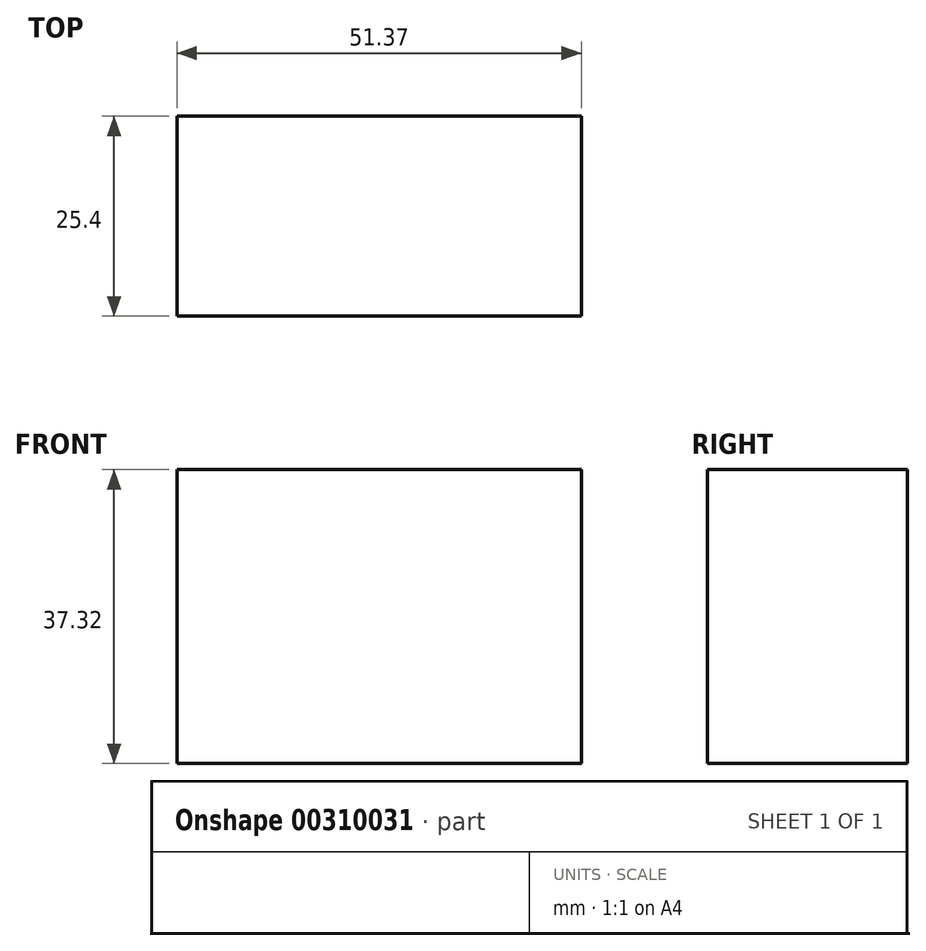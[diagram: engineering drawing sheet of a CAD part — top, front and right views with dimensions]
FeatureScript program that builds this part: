
annotation { "Feature Type Name" : "Feature", "Feature Type Description" : "" }
export const myFeature = defineFeature(function(context is Context, id is Id, definition is map)
    precondition{}
    {
        {
            var Q0;
            Q0=qCreatedBy(makeId("Front.planeOp"),FACE);
            var sketch = newSketch(context, id + "F0", { "sketchPlane" : qUnion([Q0])});
            skLineSegment(sketch, "E0", {"start": v(0, 0) * mm, "end": v(0, 37.32) * mm});
            skLineSegment(sketch, "E1", {"start": v(0, 37.32) * mm, "end": v(51.37, 37.32) * mm});
            skLineSegment(sketch, "E2", {"start": v(51.37, 37.32) * mm, "end": v(51.37, 0) * mm});
            skLineSegment(sketch, "E3", {"start": v(51.37, 0) * mm, "end": v(0, 0) * mm});
            skSolve(sketch);
        }
        {
            var Q0;
            Q0 = qSketchRegion(id + "F0", true);
            extrude(context, id + "F1", {"entities" : qUnion([Q0]), "depth" : 25.4 * mm});
        }
    });
